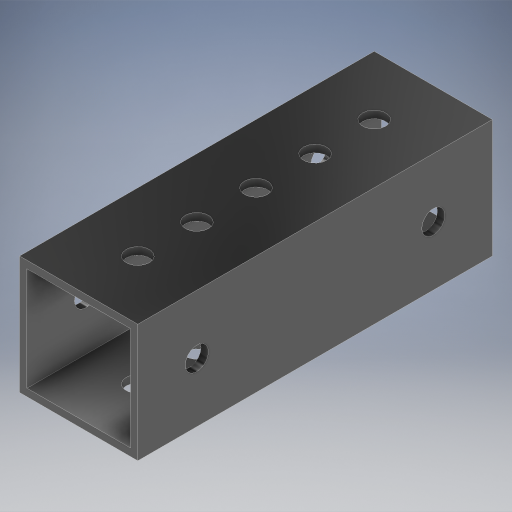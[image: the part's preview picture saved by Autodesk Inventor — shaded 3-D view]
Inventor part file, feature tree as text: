
AUTODESK INVENTOR PART (.ipt)
format: ipt  version: 2024.2 (Build 282272000, 272)  size: 709,632 bytes
history: native  units: in
note: dims shown in document units (in); Inventor stores cm internally (conversion verified against a paired STEP export)
features: other x13, extrude x9, hole x3, pattern_linear x3, mirror x3, sheet_metal_op x1, plane x1
ambient origin geometry x8: Origin, YZ Plane, XZ Plane, XY Plane, X Axis, Y Axis, Z Axis, Center Point
bodies: Solid1 (feature_tree)
feature tree (33):
  other  "Blocks"
  other  "Base Sketch"
  extrude  "Base"  Depth=1.0in
  extrude  "MAX Corner"  Depth=1.0in
  extrude  "MAX Corner Cut"  Depth=0.0625in
  extrude  "Scribe Lines"  Depth=0.0625in
  other  "Side Middle"
  other  "Top Middle"
  other  "Side Holes Sketch"
  hole  "Top Side Hole"  [1 undecoded]
  hole  "Mid Side Hole"  [1 undecoded]
  hole  "Btm Side Hole"  [1 undecoded]
  pattern_linear  "Side Holes"  Spacing1=0.04in  [1 undecoded]
  mirror  "Side Mirror"
  extrude  "MAXTube Hole"  Depth=0.04in
  extrude  "MAXTube Outside"  Depth=3.0in
  pattern_linear  "MAXTube Pattern"  Spacing1=0.0in  [1 undecoded]
  mirror  "MAXTube Mirror"
  extrude  "Left Top Hole"  Depth=3.0in
  extrude  "Mid Top Hole"  TaperAngle=0.0deg  [1 undecoded]
  extrude  "Right Top Hole"  TaperAngle=0.0deg  [1 undecoded]
  pattern_linear  "Top Holes"  Spacing1=0.005in  [1 undecoded]
  mirror  "Top Mirror"
  sheet_metal_op  "Corner"
  other  "MAXTube"
  plane  "Work Plane3"
  other  "Corner:5"
  other  "Corner:6"
  other  "Corner:7"
  other  "Corner:8"
  other  "MAXTube:1"
  other  "MAXTube:2"
  other  "MAXTube:3"
note: 8 required parameter values undecoded (feature->parameter linkage not recoverable at this tier; creation-order binding heuristic only, values carry confidence <= 0.55)
